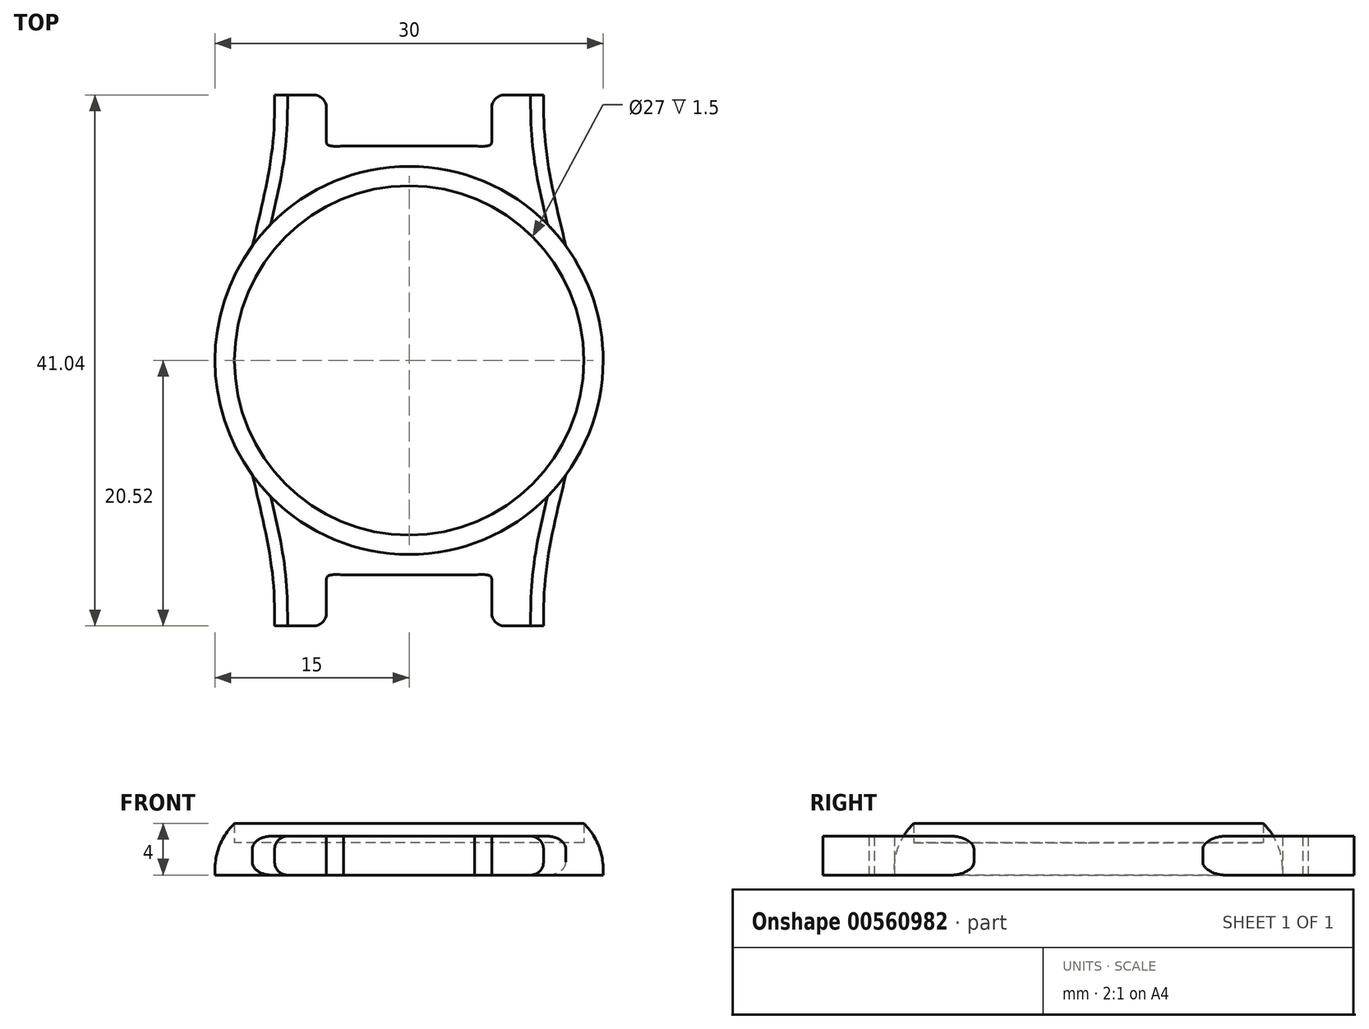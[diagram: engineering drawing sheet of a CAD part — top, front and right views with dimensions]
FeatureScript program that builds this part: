
annotation { "Feature Type Name" : "Feature", "Feature Type Description" : "" }
export const myFeature = defineFeature(function(context is Context, id is Id, definition is map)
    precondition{}
    {
        {
            var Q0;
            Q0=qCreatedBy(makeId("Top.planeOp"),FACE);
            var sketch = newSketch(context, id + "F0", { "sketchPlane" : qUnion([Q0])});
            skCircle(sketch, "E0", {"center": v(0, 0) * mm, "radius": 15 * mm});
            skFitSpline(sketch, "E1", {"points": [v(-12.11, 8.84) * mm, v(-10.61, 16.05) * mm, v(-10.4, 20.52) * mm], "startDerivative": vector(3.26, 13.56) * mm, "endDerivative": vector(0.04, 9.63) * mm});
            skLineSegment(sketch, "E2", {"start": v(-10.4, 20.52) * mm, "end": v(-6.4, 20.52) * mm});
            skLineSegment(sketch, "E3", {"start": v(-6.4, 20.52) * mm, "end": v(-6.4, 16.96) * mm});
            skFitSpline(sketch, "E4", {"points": [v(-6.4, 16.96) * mm, v(-6.28, 16.66) * mm, v(-5.06, 16.57) * mm], "startDerivative": vector(0.05, -1.03) * mm, "endDerivative": vector(2.35, 0.11) * mm});
            skLineSegment(sketch, "E5", {"start": v(-5.06, 16.57) * mm, "end": v(0, 16.57) * mm});
            skLineSegment(sketch, "E6.MirrorCS", {"start": v(5.06, 16.57) * mm, "end": v(0, 16.57) * mm});
            skFitSpline(sketch, "E7.MirrorCS", {"points": [v(6.4, 16.96) * mm, v(6.28, 16.66) * mm, v(5.06, 16.57) * mm], "startDerivative": vector(-0.05, -1.03) * mm, "endDerivative": vector(-2.35, 0.11) * mm});
            skLineSegment(sketch, "E8.MirrorCS", {"start": v(6.4, 20.52) * mm, "end": v(6.4, 16.96) * mm});
            skLineSegment(sketch, "E9.MirrorCS", {"start": v(10.4, 20.52) * mm, "end": v(6.4, 20.52) * mm});
            skFitSpline(sketch, "E10.MirrorCS", {"points": [v(12.11, 8.84) * mm, v(10.61, 16.05) * mm, v(10.4, 20.52) * mm], "startDerivative": vector(-3.26, 13.56) * mm, "endDerivative": vector(-0.04, 9.63) * mm});
            skFitSpline(sketch, "E11.MirrorCS", {"points": [v(-12.11, -8.84) * mm, v(-10.61, -16.05) * mm, v(-10.4, -20.52) * mm], "startDerivative": vector(3.26, -13.56) * mm, "endDerivative": vector(0.04, -9.63) * mm});
            skLineSegment(sketch, "E12.MirrorCS", {"start": v(-10.4, -20.52) * mm, "end": v(-6.4, -20.52) * mm});
            skLineSegment(sketch, "E13.MirrorCS", {"start": v(-6.4, -20.52) * mm, "end": v(-6.4, -16.96) * mm});
            skFitSpline(sketch, "E14.MirrorCS", {"points": [v(-6.4, -16.96) * mm, v(-6.28, -16.66) * mm, v(-5.06, -16.57) * mm], "startDerivative": vector(0.05, 1.03) * mm, "endDerivative": vector(2.35, -0.11) * mm});
            skLineSegment(sketch, "E15.MirrorCS", {"start": v(-5.06, -16.57) * mm, "end": v(0, -16.57) * mm});
            skLineSegment(sketch, "E16.MirrorCS", {"start": v(5.06, -16.57) * mm, "end": v(0, -16.57) * mm});
            skFitSpline(sketch, "E17.MirrorCS", {"points": [v(6.4, -16.96) * mm, v(6.28, -16.66) * mm, v(5.06, -16.57) * mm], "startDerivative": vector(-0.05, 1.03) * mm, "endDerivative": vector(-2.35, -0.11) * mm});
            skLineSegment(sketch, "E18.MirrorCS", {"start": v(6.4, -20.52) * mm, "end": v(6.4, -16.96) * mm});
            skLineSegment(sketch, "E19.MirrorCS", {"start": v(10.4, -20.52) * mm, "end": v(6.4, -20.52) * mm});
            skFitSpline(sketch, "E20.MirrorCS", {"points": [v(12.11, -8.84) * mm, v(10.61, -16.05) * mm, v(10.4, -20.52) * mm], "startDerivative": vector(-3.26, -13.56) * mm, "endDerivative": vector(-0.04, -9.63) * mm});
            skCircle(sketch, "E21", {"center": v(0, 0) * mm, "radius": 13.5 * mm});
            skSolve(sketch);
        }
        {
            var Q0;
            {var subQ0=sQuery(id+"F0.wireOp",EDGE,"E1");Q0=makeQuery(id+"F0.imprint","IMPRINT",FACE,{"disambiguationData":[TD([[makeQuery(id+"F0.imprint","IMPRINT",EDGE,{"derivedFrom":subQ0}),-1.0]])]});}
            var Q1;
            {var subQ0=sQuery(id+"F0.wireOp",EDGE,"E11.MirrorCS");Q1=makeQuery(id+"F0.imprint","IMPRINT",FACE,{"disambiguationData":[TD([[makeQuery(id+"F0.imprint","IMPRINT",EDGE,{"derivedFrom":subQ0}),1.0]])]});}
            extrude(context, id + "F1", {"entities" : qUnion([Q0, Q1]), "depth" : 3 * mm, "offsetDistance" : 25 * mm});
        }
        {
            var Q0;
            Q0=makeQuery(id+"F0.imprint","IMPRINT",FACE,{"disambiguationData":[TD([[makeQuery(id+"F0.imprint","IMPRINT",EDGE,{"derivedFrom":sQuery(id+"F0.wireOp",EDGE,"E21")}),-1.0]])]});
            extrude(context, id + "F2", {"entities" : qUnion([Q0]), "depth" : 4 * mm, "offsetDistance" : 25 * mm});
        }
        {
            var Q0;
            Q0=makeQuery(id+"F0.imprint","IMPRINT",FACE,{"disambiguationData":[TD([[makeQuery(id+"F0.imprint","IMPRINT",EDGE,{"derivedFrom":sQuery(id+"F0.wireOp",EDGE,"E21")}),1.0]])]});
            extrude(context, id + "F3", {"entities" : qUnion([Q0]), "operationType" : NewBodyOperationType.ADD, "depth" : 2.5 * mm, "offsetDistance" : 25 * mm});
        }
        {
            var Q0;
            Q0=makeQuery(id+"F2.opExtrude","CAP_EDGE",EDGE,{"disambiguationData":[OSD([sQuery(id+"F0.wireOp",EDGE,"E0")])],"isStart":false});
            fillet(context, id + "F4", {"entities" : qUnion([Q0]), "radius" : 5 * mm, "tangentPropagation" : true, "allowEdgeOverflow" : false});
        }
        {
            var Q0;
            Q0=makeQuery(id+"F1.opExtrude","CAP_EDGE",EDGE,{"disambiguationData":[OSD([sQuery(id+"F0.wireOp",EDGE,"E11.MirrorCS")])],"isStart":false});
            var Q1;
            Q1=makeQuery(id+"F1.opExtrude","CAP_EDGE",EDGE,{"disambiguationData":[OSD([sQuery(id+"F0.wireOp",EDGE,"E20.MirrorCS")])],"isStart":false});
            var Q2;
            Q2=makeQuery(id+"F1.opExtrude","CAP_EDGE",EDGE,{"disambiguationData":[OSD([sQuery(id+"F0.wireOp",EDGE,"E10.MirrorCS")])],"isStart":false});
            var Q3;
            Q3=makeQuery(id+"F1.opExtrude","CAP_EDGE",EDGE,{"disambiguationData":[OSD([sQuery(id+"F0.wireOp",EDGE,"E1")])],"isStart":false});
            var Q4;
            Q4=makeQuery(id+"F1.opExtrude","CAP_EDGE",EDGE,{"disambiguationData":[OSD([sQuery(id+"F0.wireOp",EDGE,"E1")])],"isStart":true});
            var Q5;
            Q5=makeQuery(id+"F1.opExtrude","CAP_EDGE",EDGE,{"disambiguationData":[OSD([sQuery(id+"F0.wireOp",EDGE,"E11.MirrorCS")])],"isStart":true});
            var Q6;
            Q6=makeQuery(id+"F1.opExtrude","CAP_EDGE",EDGE,{"disambiguationData":[OSD([sQuery(id+"F0.wireOp",EDGE,"E20.MirrorCS")])],"isStart":true});
            var Q7;
            Q7=makeQuery(id+"F1.opExtrude","CAP_EDGE",EDGE,{"disambiguationData":[OSD([sQuery(id+"F0.wireOp",EDGE,"E10.MirrorCS")])],"isStart":true});
            var Q8;
            Q8=makeQuery(id+"F1.opExtrude","SWEPT_EDGE",EDGE,{"disambiguationData":[OSD([sQuery(id+"F0.wireOp",EDGE,"E2"),sQuery(id+"F0.wireOp",EDGE,"E3")])]});
            var Q9;
            Q9=makeQuery(id+"F1.opExtrude","SWEPT_EDGE",EDGE,{"disambiguationData":[OSD([sQuery(id+"F0.wireOp",EDGE,"E8.MirrorCS"),sQuery(id+"F0.wireOp",EDGE,"E9.MirrorCS")])]});
            var Q10;
            Q10=makeQuery(id+"F1.opExtrude","SWEPT_EDGE",EDGE,{"disambiguationData":[OSD([sQuery(id+"F0.wireOp",EDGE,"E12.MirrorCS"),sQuery(id+"F0.wireOp",EDGE,"E13.MirrorCS")])]});
            var Q11;
            Q11=makeQuery(id+"F1.opExtrude","SWEPT_EDGE",EDGE,{"disambiguationData":[OSD([sQuery(id+"F0.wireOp",EDGE,"E18.MirrorCS"),sQuery(id+"F0.wireOp",EDGE,"E19.MirrorCS")])]});
            fillet(context, id + "F5", {"entities" : qUnion([Q0, Q1, Q2, Q3, Q4, Q5, Q6, Q7, Q8, Q9, Q10, Q11]), "radius" : 1 * mm, "tangentPropagation" : true, "allowEdgeOverflow" : false});
        }
    });
